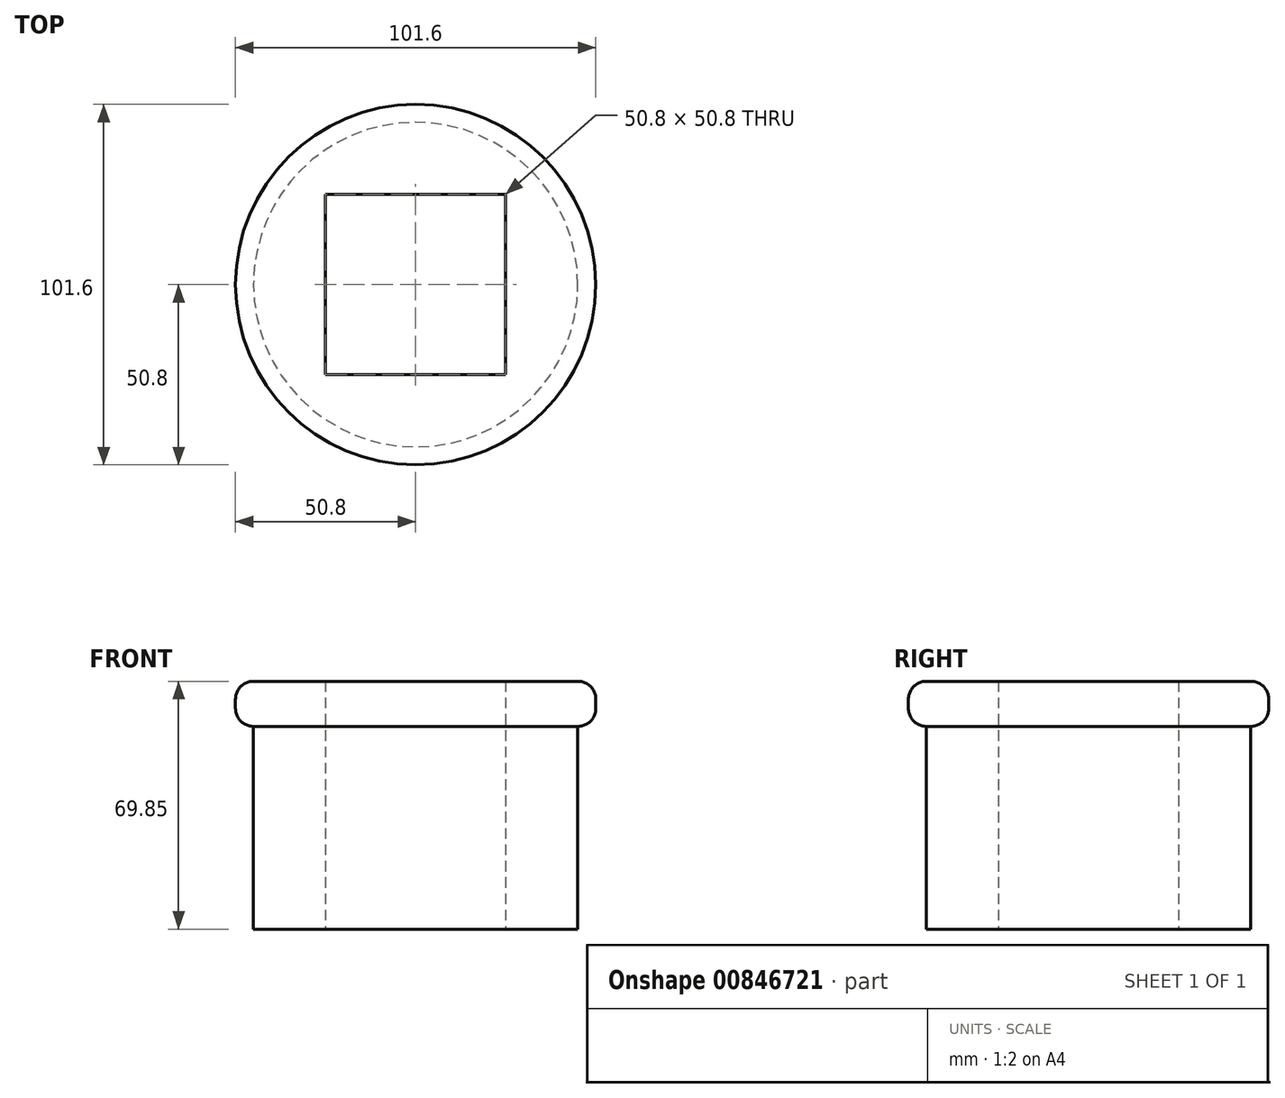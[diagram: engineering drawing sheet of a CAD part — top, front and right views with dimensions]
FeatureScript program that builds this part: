
annotation { "Feature Type Name" : "Feature", "Feature Type Description" : "" }
export const myFeature = defineFeature(function(context is Context, id is Id, definition is map)
    precondition{}
    {
        {
            var Q0;
            Q0=qCreatedBy(makeId("Top.planeOp"),FACE);
            var sketch = newSketch(context, id + "F0", { "sketchPlane" : qUnion([Q0])});
            skLineSegment(sketch, "E0.bottom", {"start": v(25.4, 25.4) * mm, "end": v(-25.4, 25.4) * mm});
            skLineSegment(sketch, "E0.top", {"start": v(25.4, -25.4) * mm, "end": v(-25.4, -25.4) * mm});
            skLineSegment(sketch, "E0.left", {"start": v(25.4, 25.4) * mm, "end": v(25.4, -25.4) * mm});
            skLineSegment(sketch, "E0.right", {"start": v(-25.4, 25.4) * mm, "end": v(-25.4, -25.4) * mm});
            skPoint(sketch, "E0.middle", {"position": v(0, 0) * mm});
            skCircle(sketch, "E1", {"center": v(0, 0) * mm, "radius": 50.8 * mm});
            skSolve(sketch);
        }
        {
            var Q0;
            Q0=makeQuery(id+"F0.imprint","IMPRINT",FACE,{"disambiguationData":[TD([[makeQuery(id+"F0.imprint","IMPRINT",EDGE,{"derivedFrom":sQuery(id+"F0.wireOp",EDGE,"E0.bottom")}),-1.0]])]});
            extrude(context, id + "F1", {"entities" : qUnion([Q0]), "depth" : 12.7 * mm, "offsetDistance" : 25.4 * mm});
        }
        {
            var Q0;
            Q0=makeQuery(id+"F1.opExtrude","SWEPT_FACE",FACE,{"disambiguationData":[OSD([sQuery(id+"F0.wireOp",EDGE,"E1")])]});
            fillet(context, id + "F2", {"entities" : qUnion([Q0]), "radius" : 5.08 * mm, "tangentPropagation" : true, "allowEdgeOverflow" : false});
        }
        {
            var Q0;
            Q0=makeQuery(id+"F1.opExtrude","CAP_FACE",FACE,{"disambiguationData":[OSD([sQuery(id+"F0.wireOp",EDGE,"E0.bottom"),sQuery(id+"F0.wireOp",EDGE,"E0.top"),sQuery(id+"F0.wireOp",EDGE,"E0.left"),sQuery(id+"F0.wireOp",EDGE,"E0.right"),sQuery(id+"F0.wireOp",EDGE,"E1")])],"isStart":true});
            extrude(context, id + "F3", {"entities" : qUnion([Q0]), "operationType" : NewBodyOperationType.ADD, "depth" : 57.15 * mm, "offsetDistance" : 25.4 * mm});
        }
    });
